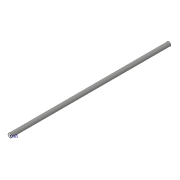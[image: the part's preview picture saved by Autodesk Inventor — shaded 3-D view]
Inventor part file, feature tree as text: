
AUTODESK INVENTOR PART (.ipt)
format: ipt  version: 2019 (Build 230136000, 136)  size: 90,112 bytes
history: native  units: mm
features: sketch x4, extrude x3, thread x1
ambient origin geometry x8: Origin, YZ Plane, XZ Plane, XY Plane, X Axis, Y Axis, Z Axis, Center Point
bodies: Solid1 (feature_tree)
feature tree (8):
  extrude  "Extrusion1"  Depth=340.0mm TaperAngle=0.0deg
  thread  "Thread1"  [1 undecoded]
  extrude  "Extrusion2"  Depth=5.0mm
  sketch  "Sketch3"  dims[d10=3.0mm d11=6.5mm]
  extrude  "Extrusion3"  Depth=6.5mm
  sketch  "Sketch1"  dims[d0=9.0mm d1=340.0mm d2=0.0mm d3=10.0mm d4=0.0mm]
  sketch  "Sketch2"  dims[d7=0.0mm d8=0.0mm d9=5.0mm]
  sketch  "Sketch4"  dims[d12=5.0mm d13=3.0mm d14=10.0mm d15=0.0mm]
note: 1 required parameter value undecoded (feature->parameter linkage not recoverable at this tier; creation-order binding heuristic only, values carry confidence <= 0.55)
